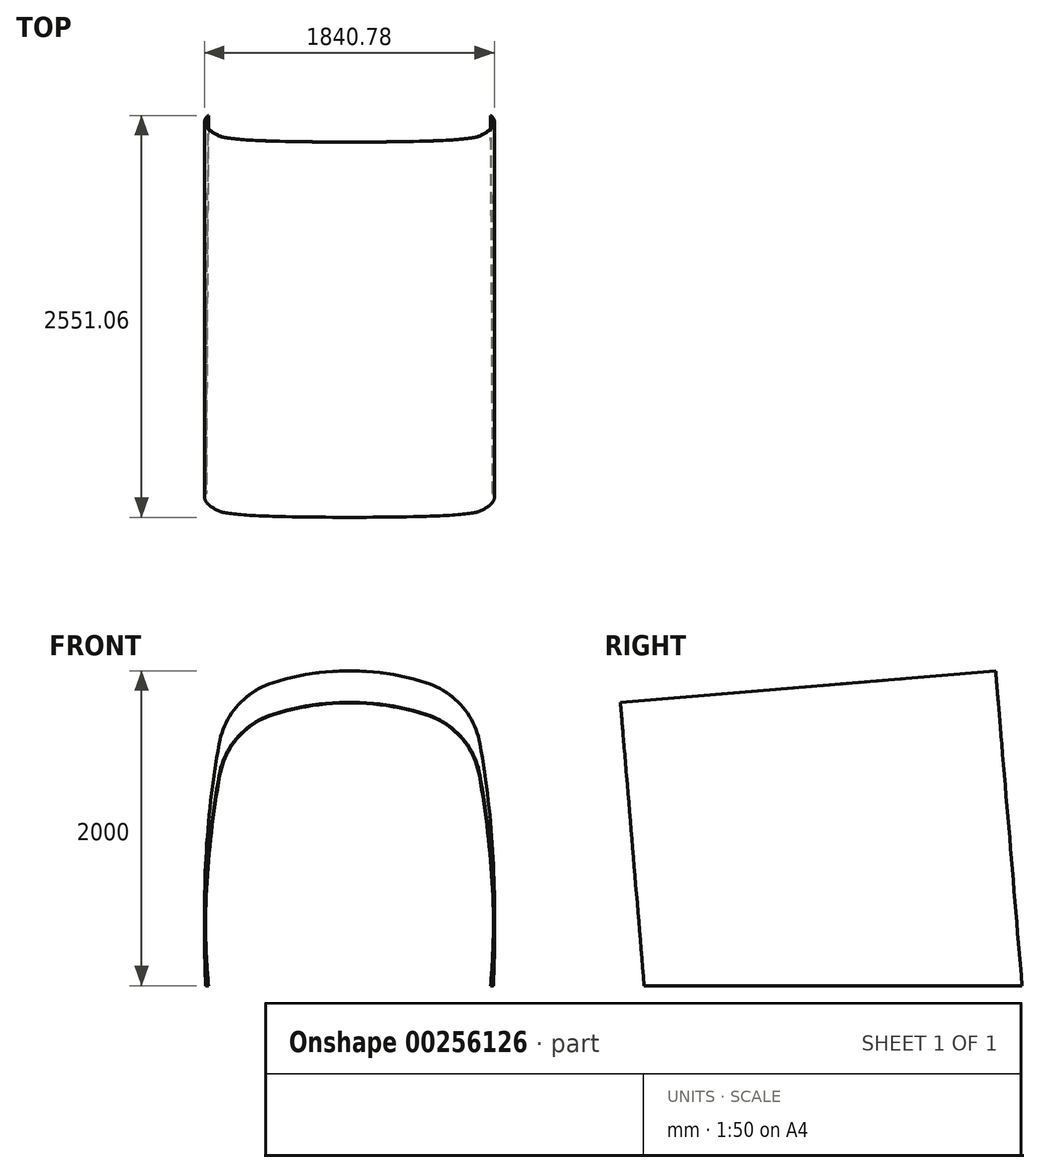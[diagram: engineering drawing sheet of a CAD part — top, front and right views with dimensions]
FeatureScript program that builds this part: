
annotation { "Feature Type Name" : "Feature", "Feature Type Description" : "" }
export const myFeature = defineFeature(function(context is Context, id is Id, definition is map)
    precondition{}
    {
        {
            var Q0;
            Q0=qCreatedBy(makeId("Right.planeOp"),FACE);
            var sketch = newSketch(context, id + "F0", { "sketchPlane" : qUnion([Q0])});
            skLineSegment(sketch, "E0", {"start": v(0, 0) * mm, "end": v(-167.84, 2000) * mm, "construction": true});
            skLineSegment(sketch, "E1", {"start": v(-167.84, 2000) * mm, "end": v(-2551.06, 1800) * mm, "construction": true});
            skLineSegment(sketch, "E2", {"start": v(-2551.06, 1800) * mm, "end": v(-2400, 0) * mm, "construction": true});
            skLineSegment(sketch, "E3", {"start": v(-2400, 0) * mm, "end": v(0, 0) * mm, "construction": true});
            skSolve(sketch);
        }
        {
            var Q0;
            Q0=sQuery(id+"F0.wireOp",EDGE,"E0");
            cPlane(context, id + "F1", {"entities" : qUnion([Q0]), "cplaneType" : CPlaneType.LINE_ANGLE, "offset" : 25 * mm, "angle" : 90 * degree, "width" : 150 * mm, "height" : 150 * mm});
        }
        {
            var Q0;
            Q0=qCreatedBy(id+"F1.planeOp",FACE);
            var sketch = newSketch(context, id + "F2", { "sketchPlane" : qUnion([Q0])});
            skLineSegment(sketch, "E4", {"start": v(-900, 0) * mm, "end": v(900, 0) * mm});
            skLineSegment(sketch, "E5", {"start": v(-775, 1807.03) * mm, "end": v(775, 1807.03) * mm, "construction": true});
            skLineSegment(sketch, "E6", {"start": v(0, 0) * mm, "end": v(0, 1807.03) * mm, "construction": true});
            skArc(sketch, "E7", {"start": v(775, 1807.03) * mm, "mid": v(0, 2007.03) * mm, "end": v(-775, 1807.03) * mm});
            skArc(sketch, "E8", {"start": v(-775, 1807.03) * mm, "mid": v(-906.08, 908.26) * mm, "end": v(-900, 0) * mm});
            skArc(sketch, "E9", {"start": v(900, 0) * mm, "mid": v(906.08, 908.26) * mm, "end": v(775, 1807.03) * mm});
            skSolve(sketch);
        }
        {
            var Q0;
            Q0=makeQuery(id+"F2.imprint","IMPRINT",FACE,{"disambiguationData":[TD([[makeQuery(id+"F2.imprint","IMPRINT",EDGE,{"derivedFrom":sQuery(id+"F2.wireOp",EDGE,"E4")}),1.0]])]});
            var Q1;
            Q1=sQuery(id+"F0.wireOp",VERTEX,"E2.start");
            extrude(context, id + "F3", {"entities" : qUnion([Q0]), "endBound" : BoundingType.UP_TO_VERTEX, "oppositeDirection" : true, "endBoundEntityVertex" : qUnion([Q1]), "depth" : 25 * mm});
        }
        {
            var Q0;
            Q0=makeQuery(id+"F3.opExtrude","SWEPT_EDGE",EDGE,{"disambiguationData":[OSD([sQuery(id+"F2.wireOp",EDGE,"E7"),sQuery(id+"F2.wireOp",EDGE,"E8")])]});
            var Q1;
            Q1=makeQuery(id+"F3.opExtrude","SWEPT_EDGE",EDGE,{"disambiguationData":[OSD([sQuery(id+"F2.wireOp",EDGE,"E7"),sQuery(id+"F2.wireOp",EDGE,"E9")])]});
            fillet(context, id + "F4", {"entities" : qUnion([Q0, Q1]), "radius" : 500 * mm, "tangentPropagation" : true, "allowEdgeOverflow" : false});
        }
        {
            var Q0;
            Q0=qCreatedBy(makeId("Right.planeOp"),FACE);
            var sketch = newSketch(context, id + "F5", { "sketchPlane" : qUnion([Q0])});
            skLineSegment(sketch, "E10", {"start": v(0, 0) * mm, "end": v(-3357.93, 0) * mm});
            skLineSegment(sketch, "E11", {"start": v(-3357.93, 0) * mm, "end": v(-3357.93, -1677.52) * mm});
            skLineSegment(sketch, "E12", {"start": v(-3357.93, -1677.52) * mm, "end": v(0, -1677.52) * mm});
            skLineSegment(sketch, "E13", {"start": v(0, -1677.52) * mm, "end": v(0, 0) * mm});
            skSolve(sketch);
        }
        {
            var Q0;
            Q0=makeQuery(id+"F5.imprint","IMPRINT",FACE,{"disambiguationData":[TD([[makeQuery(id+"F5.imprint","IMPRINT",EDGE,{"derivedFrom":sQuery(id+"F5.wireOp",EDGE,"E10")}),1.0]])]});
            extrude(context, id + "F6", {"entities" : qUnion([Q0]), "operationType" : NewBodyOperationType.REMOVE, "endBound" : BoundingType.SYMMETRIC, "oppositeDirection" : true, "depth" : 2000 * mm});
        }
        {
            var Q0;
            Q0=makeQuery(id+"F3.opExtrude","CAP_FACE",FACE,{"disambiguationData":[OSD([sQuery(id+"F2.wireOp",EDGE,"E4"),sQuery(id+"F2.wireOp",EDGE,"E7"),sQuery(id+"F2.wireOp",EDGE,"E8"),sQuery(id+"F2.wireOp",EDGE,"E9")])],"isStart":true});
            var Q1;
            Q1=makeQuery(id+"F3.opExtrude","CAP_FACE",FACE,{"disambiguationData":[OSD([sQuery(id+"F2.wireOp",EDGE,"E4"),sQuery(id+"F2.wireOp",EDGE,"E7"),sQuery(id+"F2.wireOp",EDGE,"E8"),sQuery(id+"F2.wireOp",EDGE,"E9")])],"isStart":false});
            var Q2;
            Q2=makeQuery(id+"F6.boolean.opBoolean","COPY",FACE,{"derivedFrom":makeQuery(id+"F6.opExtrude","SWEPT_FACE",FACE,{"disambiguationData":[OSD([sQuery(id+"F5.wireOp",EDGE,"E10")])]})});
            shell(context, id + "F7", {"entities" : qUnion([Q0, Q1, Q2]), "thickness" : 4 * mm});
        }
    });
